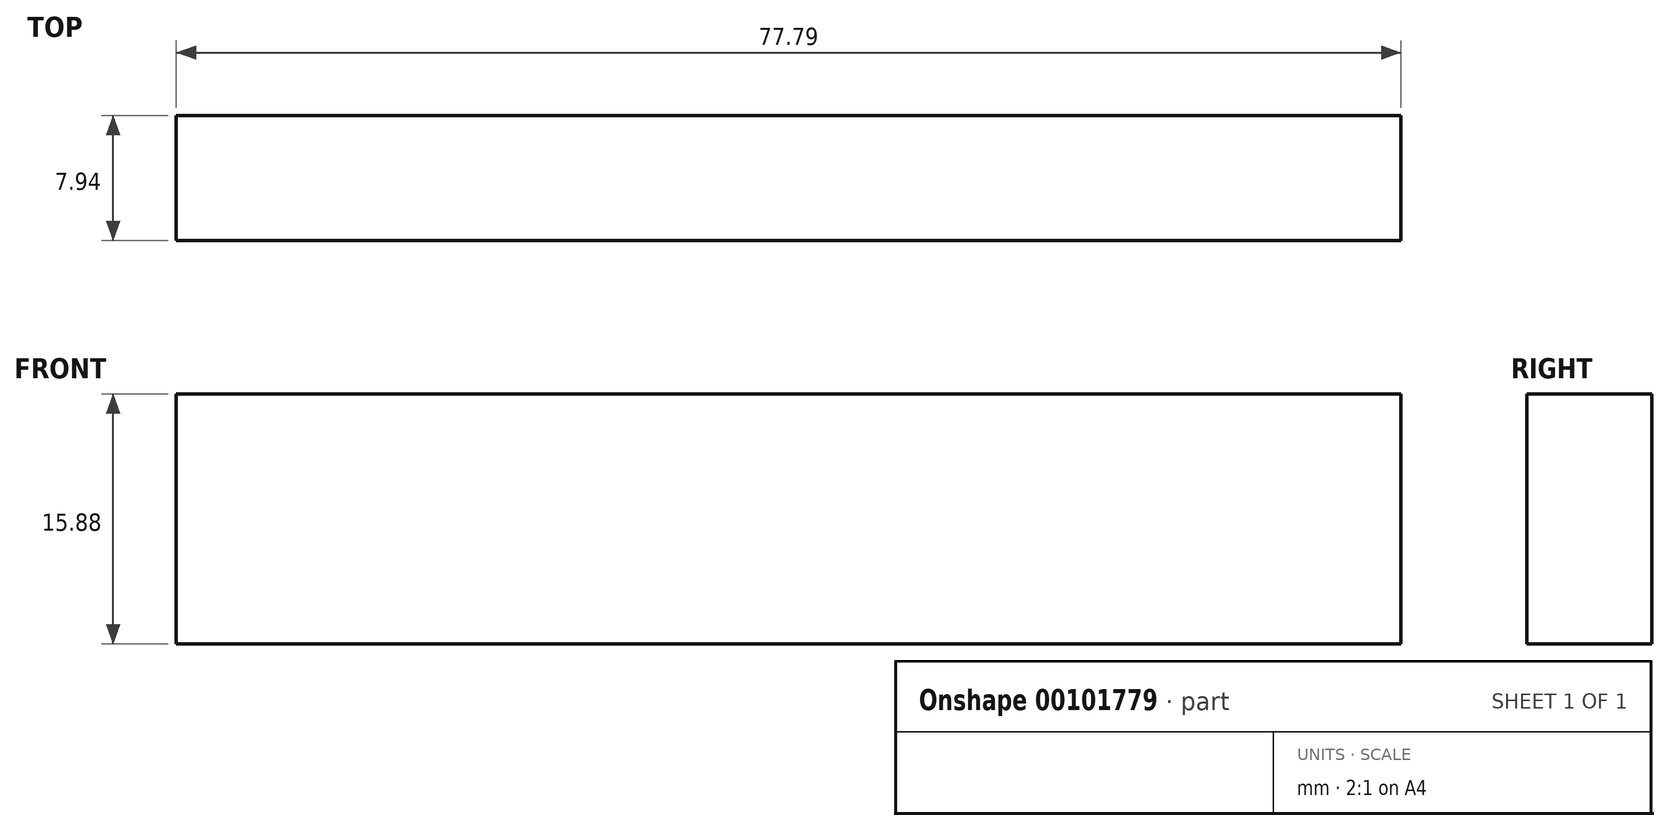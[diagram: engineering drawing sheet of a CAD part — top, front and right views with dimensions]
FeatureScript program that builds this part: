
annotation { "Feature Type Name" : "Feature", "Feature Type Description" : "" }
export const myFeature = defineFeature(function(context is Context, id is Id, definition is map)
    precondition{}
    {
        {
            var Q0;
            Q0=qCreatedBy(makeId("Front.planeOp"),FACE);
            var sketch = newSketch(context, id + "F0", { "sketchPlane" : qUnion([Q0])});
            skLineSegment(sketch, "E0.bottom", {"start": v(-41.78, 15.88) * mm, "end": v(36.01, 15.88) * mm});
            skLineSegment(sketch, "E0.top", {"start": v(-41.78, 0) * mm, "end": v(36.01, 0) * mm});
            skLineSegment(sketch, "E0.left", {"start": v(-41.78, 15.88) * mm, "end": v(-41.78, 0) * mm});
            skLineSegment(sketch, "E0.right", {"start": v(36.01, 15.87) * mm, "end": v(36.01, 0) * mm});
            skSolve(sketch);
        }
        {
            var Q0;
            Q0=makeQuery(id+"F0.imprint","IMPRINT",FACE,{"disambiguationData":[TD([[makeQuery(id+"F0.imprint","IMPRINT",EDGE,{"derivedFrom":sQuery(id+"F0.wireOp",EDGE,"E0.bottom")}),-1.0]])]});
            extrude(context, id + "F1", {"entities" : qUnion([Q0]), "depth" : 7.94 * mm});
        }
    });
